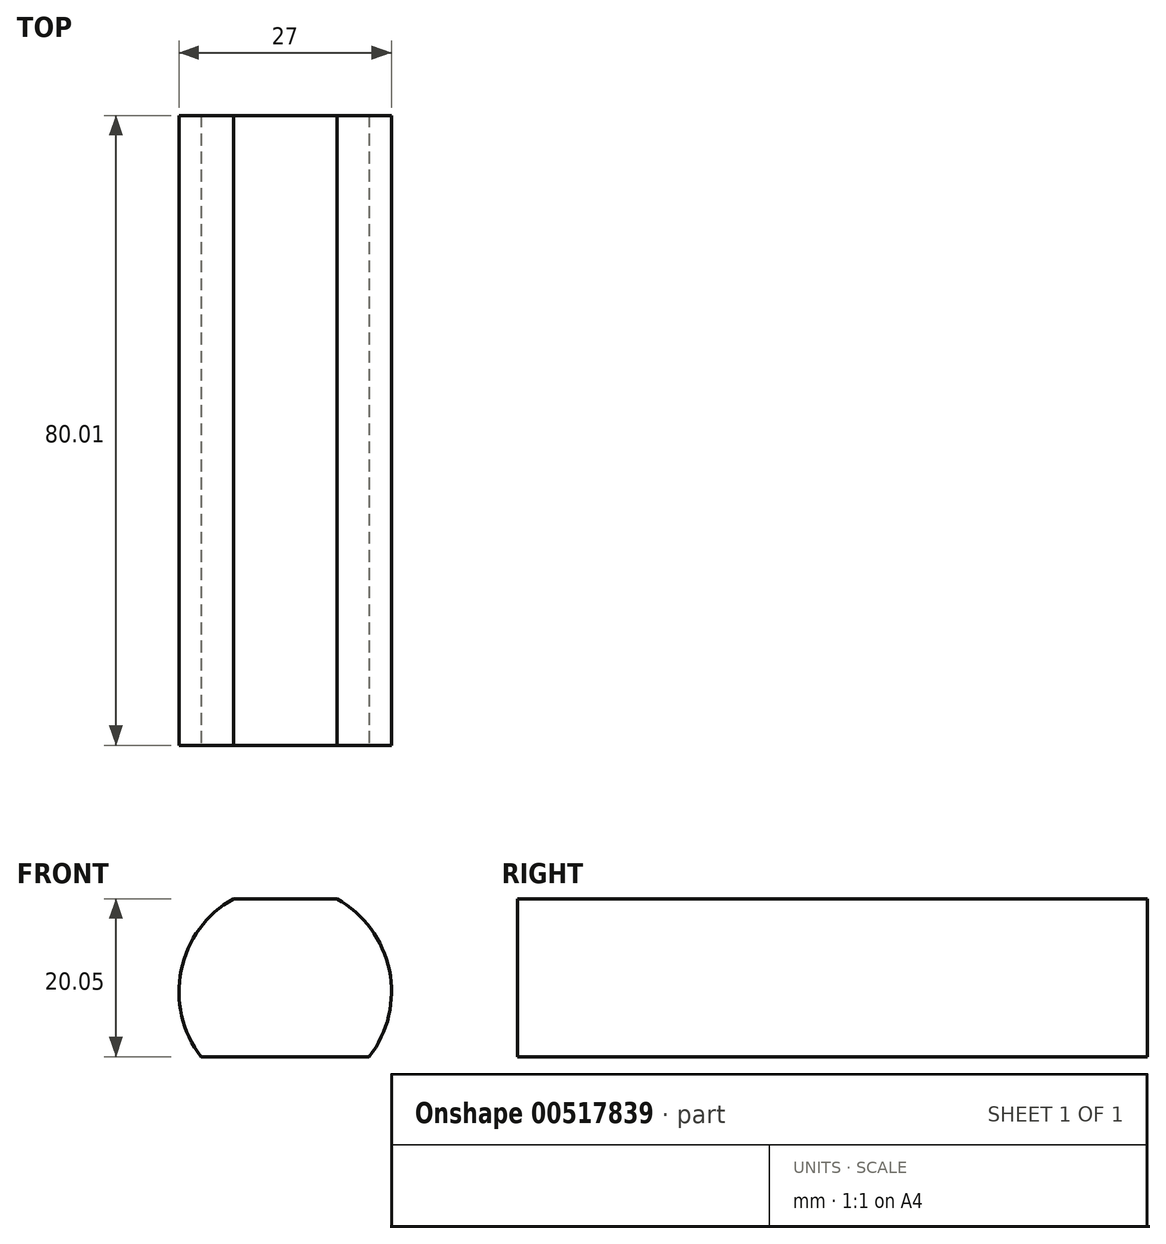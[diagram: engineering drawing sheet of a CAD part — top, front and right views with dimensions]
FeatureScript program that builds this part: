
annotation { "Feature Type Name" : "Feature", "Feature Type Description" : "" }
export const myFeature = defineFeature(function(context is Context, id is Id, definition is map)
    precondition{}
    {
        {
            var Q0;
            Q0=qCreatedBy(makeId("Front.planeOp"),FACE);
            var sketch = newSketch(context, id + "F0", { "sketchPlane" : qUnion([Q0])});
            skCircle(sketch, "E0", {"center": v(0, 0) * mm, "radius": 13.5 * mm});
            skLineSegment(sketch, "E1", {"start": v(10.69, -8.25) * mm, "end": v(-10.69, -8.25) * mm});
            skLineSegment(sketch, "E2", {"start": v(-6.56, 11.8) * mm, "end": v(6.56, 11.8) * mm});
            skArc(sketch, "E3", {"start": v(-6.56, 11.8) * mm, "mid": v(-13.22, 2.72) * mm, "end": v(-10.69, -8.25) * mm});
            skArc(sketch, "E4", {"start": v(6.56, 11.8) * mm, "mid": v(13.22, 2.72) * mm, "end": v(10.69, -8.25) * mm});
            skSolve(sketch);
        }
        {
            var Q0;
            Q0=sQuery(id+"F0.wireOp",EDGE,"E3");
            var Q1;
            Q1=sQuery(id+"F0.wireOp",EDGE,"E2");
            var Q2;
            Q2=sQuery(id+"F0.wireOp",EDGE,"E4");
            var Q3;
            Q3=sQuery(id+"F0.wireOp",EDGE,"E1");
            extrude(context, id + "F1", {"bodyType" : ToolBodyType.SURFACE, "surfaceEntities" : qUnion([Q0, Q1, Q2, Q3]), "depth" : 80 * mm, "offsetDistance" : 25.4 * mm});
        }
    });
